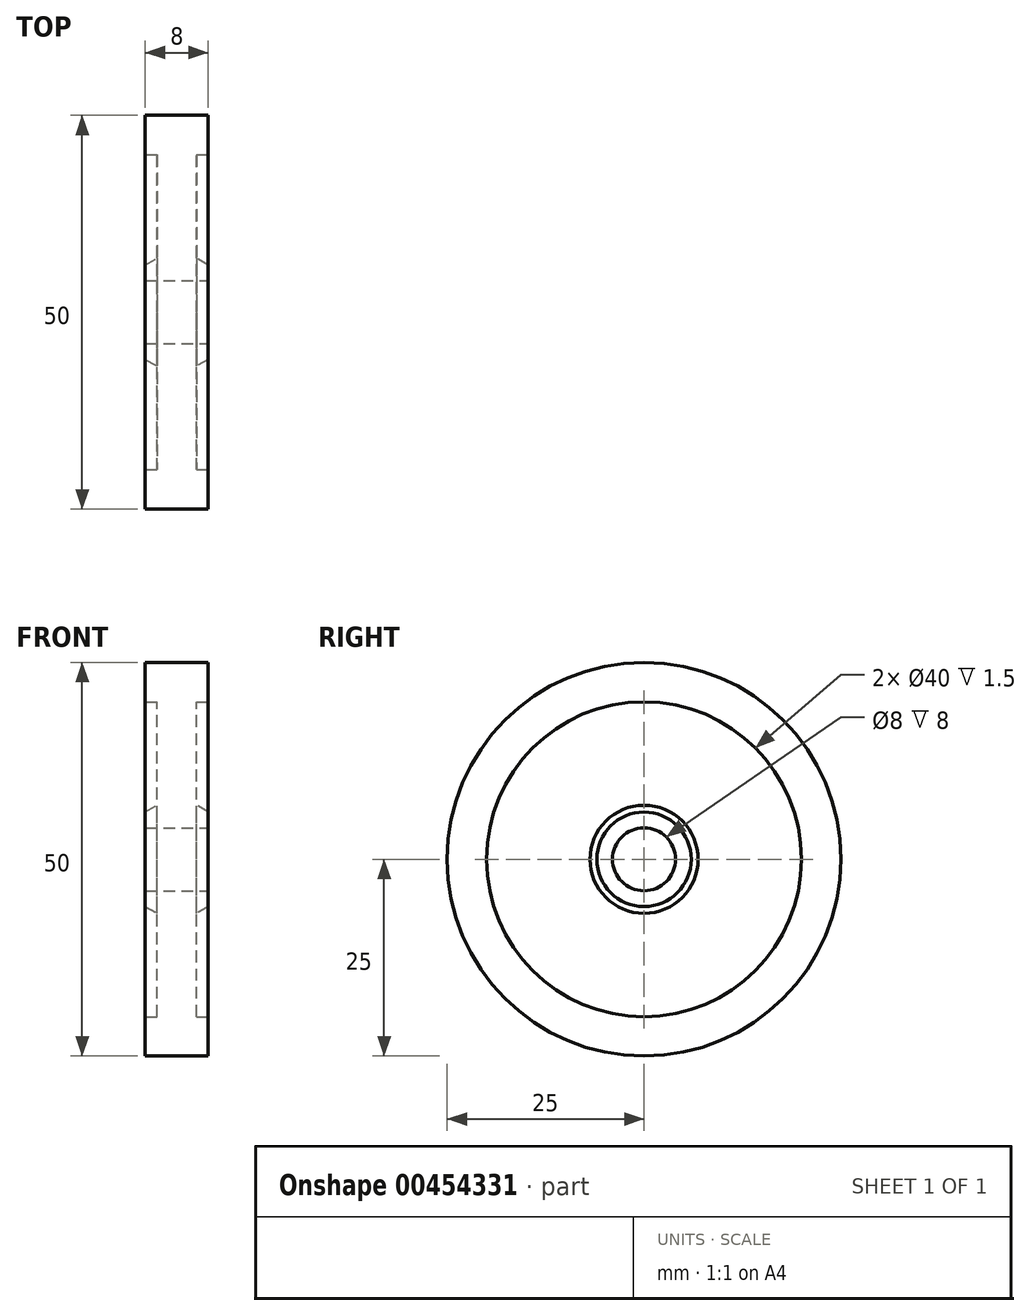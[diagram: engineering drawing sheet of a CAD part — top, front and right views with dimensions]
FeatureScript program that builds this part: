
annotation { "Feature Type Name" : "Feature", "Feature Type Description" : "" }
export const myFeature = defineFeature(function(context is Context, id is Id, definition is map)
    precondition{}
    {
        {
            var Q0;
            Q0=qCreatedBy(makeId("Front.planeOp"),FACE);
            var sketch = newSketch(context, id + "F0", { "sketchPlane" : qUnion([Q0])});
            skLineSegment(sketch, "E0", {"start": v(0, 0) * mm, "end": v(-17.98, 0) * mm, "construction": true});
            skLineSegment(sketch, "E1", {"start": v(0, 0) * mm, "end": v(0, 30.48) * mm, "construction": true});
            skLineSegment(sketch, "E2", {"start": v(0, 4) * mm, "end": v(-4, 4) * mm});
            skLineSegment(sketch, "E3", {"start": v(-4, 4) * mm, "end": v(-4, 6) * mm});
            skLineSegment(sketch, "E4", {"start": v(-4, 6) * mm, "end": v(-2.5, 6.87) * mm});
            skLineSegment(sketch, "E5", {"start": v(-2.5, 6.87) * mm, "end": v(-2.5, 20) * mm});
            skLineSegment(sketch, "E6", {"start": v(-2.5, 20) * mm, "end": v(-4, 20) * mm});
            skLineSegment(sketch, "E7", {"start": v(-4, 20) * mm, "end": v(-4, 25) * mm});
            skLineSegment(sketch, "E8", {"start": v(-4, 25) * mm, "end": v(0, 25) * mm});
            skLineSegment(sketch, "E9.MirrorCS", {"start": v(2.5, 20) * mm, "end": v(4, 20) * mm});
            skLineSegment(sketch, "E10.MirrorCS", {"start": v(4, 4) * mm, "end": v(4, 6) * mm});
            skLineSegment(sketch, "E11.MirrorCS", {"start": v(4, 25) * mm, "end": v(0, 25) * mm});
            skLineSegment(sketch, "E12.MirrorCS", {"start": v(4, 20) * mm, "end": v(4, 25) * mm});
            skLineSegment(sketch, "E13.MirrorCS", {"start": v(0, 4) * mm, "end": v(4, 4) * mm});
            skLineSegment(sketch, "E14.MirrorCS", {"start": v(2.5, 6.87) * mm, "end": v(2.5, 20) * mm});
            skLineSegment(sketch, "E15.MirrorCS", {"start": v(4, 6) * mm, "end": v(2.5, 6.87) * mm});
            skSolve(sketch);
        }
        {
            var Q0;
            Q0 = qSketchRegion(id + "F0", true);
            var Q1;
            Q1=sQuery(id+"F0.wireOp",EDGE,"E0");
            revolve(context, id + "F1", {"entities" : qUnion([Q0]), "axis" : qUnion([Q1]), "revolveType" : RevolveType.FULL});
        }
    });
